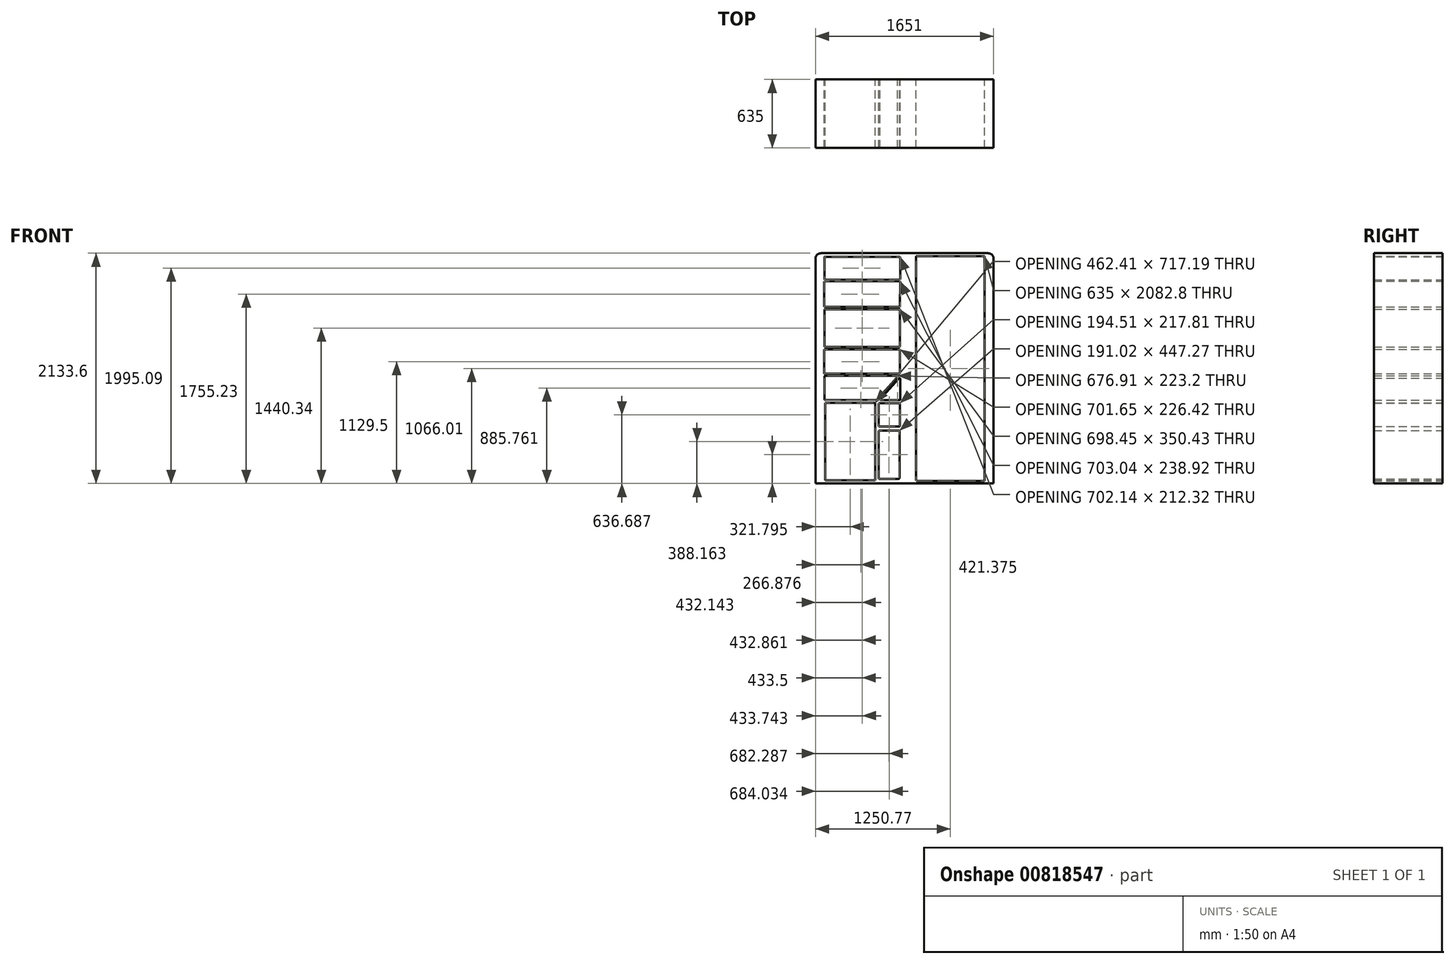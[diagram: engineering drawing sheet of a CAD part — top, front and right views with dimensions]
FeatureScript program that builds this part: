
annotation { "Feature Type Name" : "Feature", "Feature Type Description" : "" }
export const myFeature = defineFeature(function(context is Context, id is Id, definition is map)
    precondition{}
    {
        {
            var Q0;
            Q0=qCreatedBy(makeId("Front.planeOp"),FACE);
            var sketch = newSketch(context, id + "F0", { "sketchPlane" : qUnion([Q0])});
            skLineSegment(sketch, "E0.bottom", {"start": v(825.5, -1066.8) * mm, "end": v(-825.5, -1066.8) * mm});
            skLineSegment(sketch, "E0.top", {"start": v(774.7, 1066.8) * mm, "end": v(-774.7, 1066.8) * mm});
            skLineSegment(sketch, "E0.left", {"start": v(825.5, -1066.8) * mm, "end": v(825.5, 1016) * mm});
            skLineSegment(sketch, "E0.right", {"start": v(-825.5, -1066.8) * mm, "end": v(-825.5, 1016) * mm});
            skPoint(sketch, "E0.middle", {"position": v(0, 0) * mm});
            skLineSegment(sketch, "E1.bottom", {"start": v(114.12, 1040.61) * mm, "end": v(736.42, 1040.61) * mm});
            skLineSegment(sketch, "E1.top", {"start": v(114.12, -1042.19) * mm, "end": v(736.42, -1042.19) * mm});
            skLineSegment(sketch, "E1.left", {"start": v(107.77, 1034.26) * mm, "end": v(107.77, -1035.84) * mm});
            skLineSegment(sketch, "E1.right", {"start": v(742.77, 1034.26) * mm, "end": v(742.77, -1035.84) * mm});
            skPoint(sketch, "E2.oppositeSnap0", {"position": v(0, -1066.8) * mm});
            skLineSegment(sketch, "E2.bottom", {"start": v(-787.4, 1045.57) * mm, "end": v(0, 1045.57) * mm});
            skLineSegment(sketch, "E2.top", {"start": v(-787.4, -1037.23) * mm, "end": v(0, -1037.23) * mm});
            skLineSegment(sketch, "E2.left", {"start": v(-787.4, 1045.57) * mm, "end": v(-787.4, -1037.23) * mm});
            skLineSegment(sketch, "E2.right", {"start": v(0, 1045.57) * mm, "end": v(0, -1037.23) * mm});
            skLineSegment(sketch, "E3.bottom", {"start": v(-752.96, -302.88) * mm, "end": v(-32.15, -302.88) * mm});
            skLineSegment(sketch, "E3.top", {"start": v(-752.96, -1037.23) * mm, "end": v(-32.15, -1037.23) * mm});
            skLineSegment(sketch, "E3.left", {"start": v(-752.96, -302.88) * mm, "end": v(-752.96, -1037.23) * mm});
            skLineSegment(sketch, "E3.right", {"start": v(-32.15, -302.88) * mm, "end": v(-32.15, -1037.23) * mm});
            skLineSegment(sketch, "E4", {"start": v(-252.12, -302.88) * mm, "end": v(-252.12, -1037.23) * mm});
            skLineSegment(sketch, "E5", {"start": v(-252.12, -560.07) * mm, "end": v(-32.15, -560.07) * mm});
            skLineSegment(sketch, "E6.bottom", {"start": v(-752.96, 1045.57) * mm, "end": v(-32.15, 1045.57) * mm});
            skLineSegment(sketch, "E6.left", {"start": v(-752.96, 1045.57) * mm, "end": v(-752.96, -302.88) * mm});
            skLineSegment(sketch, "E6.right", {"start": v(-32.15, 1045.57) * mm, "end": v(-32.15, -302.88) * mm});
            skLineSegment(sketch, "E7", {"start": v(-752.96, 813.88) * mm, "end": v(-32.15, 813.88) * mm});
            skLineSegment(sketch, "E8", {"start": v(-752.96, 560.07) * mm, "end": v(-32.15, 560.07) * mm});
            skLineSegment(sketch, "E9", {"start": v(-752.96, 187.82) * mm, "end": v(-32.15, 187.82) * mm});
            skLineSegment(sketch, "E10", {"start": v(-752.96, -59.22) * mm, "end": v(-32.15, -59.22) * mm});
            skLineSegment(sketch, "E11", {"start": v(-252.12, -302.88) * mm, "end": v(-32.15, -59.22) * mm});
            skLineSegment(sketch, "E12.left", {"start": v(-752.96, 1016.92) * mm, "end": v(-752.96, 854.49) * mm});
            skLineSegment(sketch, "E12.right", {"start": v(-40.93, 1028.1) * mm, "end": v(-40.93, 828.48) * mm});
            skLineSegment(sketch, "E13.left", {"start": v(-752.96, 780.04) * mm, "end": v(-752.96, 593.91) * mm});
            skLineSegment(sketch, "E14.bottom", {"start": v(-734.63, 548.76) * mm, "end": v(-48.88, 548.76) * mm});
            skLineSegment(sketch, "E14.top", {"start": v(-734.63, 198.33) * mm, "end": v(-48.88, 198.33) * mm});
            skLineSegment(sketch, "E14.left", {"start": v(-740.98, 542.4) * mm, "end": v(-740.98, 204.68) * mm});
            skLineSegment(sketch, "E14.right", {"start": v(-42.53, 542.4) * mm, "end": v(-42.53, 204.68) * mm});
            skLineSegment(sketch, "E15.bottom", {"start": v(-737.83, 175.9) * mm, "end": v(-48.88, 175.9) * mm});
            skLineSegment(sketch, "E15.top", {"start": v(-737.83, -50.51) * mm, "end": v(-48.88, -50.51) * mm});
            skLineSegment(sketch, "E15.left", {"start": v(-744.18, 169.56) * mm, "end": v(-744.18, -44.16) * mm});
            skLineSegment(sketch, "E15.right", {"start": v(-42.53, 169.56) * mm, "end": v(-42.53, -44.16) * mm});
            skLineSegment(sketch, "E16.bottom", {"start": v(-728.56, -320.04) * mm, "end": v(-278.85, -320.04) * mm});
            skLineSegment(sketch, "E16.top", {"start": v(-734.9, -1037.23) * mm, "end": v(-272.5, -1037.23) * mm});
            skLineSegment(sketch, "E16.left", {"start": v(-734.9, -326.4) * mm, "end": v(-734.9, -1037.23) * mm});
            skLineSegment(sketch, "E16.right", {"start": v(-272.5, -326.4) * mm, "end": v(-272.5, -1037.23) * mm});
            skLineSegment(sketch, "E17.bottom", {"start": v(-232.37, -321.2) * mm, "end": v(-50.56, -321.2) * mm});
            skLineSegment(sketch, "E17.top", {"start": v(-232.37, -539.02) * mm, "end": v(-50.56, -539.02) * mm});
            skLineSegment(sketch, "E17.left", {"start": v(-238.72, -327.56) * mm, "end": v(-238.72, -532.67) * mm});
            skLineSegment(sketch, "E17.right", {"start": v(-44.2, -327.56) * mm, "end": v(-44.2, -532.67) * mm});
            skLineSegment(sketch, "E18.bottom", {"start": v(-232.37, -576.3) * mm, "end": v(-54.05, -576.3) * mm});
            skLineSegment(sketch, "E18.top", {"start": v(-232.37, -1023.56) * mm, "end": v(-54.05, -1023.56) * mm});
            skLineSegment(sketch, "E18.left", {"start": v(-238.72, -582.64) * mm, "end": v(-238.72, -1017.2) * mm});
            skLineSegment(sketch, "E18.right", {"start": v(-47.7, -582.64) * mm, "end": v(-47.7, -1017.2) * mm});
            skLineSegment(sketch, "E19", {"start": v(-742.58, -75.8) * mm, "end": v(-742.58, -286.29) * mm});
            skLineSegment(sketch, "E20", {"start": v(-736.23, -69.44) * mm, "end": v(-71.96, -69.44) * mm});
            skLineSegment(sketch, "E21", {"start": v(-67.25, -80.05) * mm, "end": v(-255.86, -288.97) * mm});
            skLineSegment(sketch, "E22", {"start": v(-260.56, -291.07) * mm, "end": v(-736.21, -292.64) * mm});
            skLineSegment(sketch, "E23", {"start": v(-40.13, -96.35) * mm, "end": v(-40.13, -286.34) * mm});
            skLineSegment(sketch, "E24", {"start": v(-51.2, -92.1) * mm, "end": v(-224.7, -284.28) * mm});
            skLineSegment(sketch, "E25", {"start": v(-46.4, -292.69) * mm, "end": v(-219.9, -294.88) * mm});
            skLineSegment(sketch, "E26", {"start": v(-47.28, 1034.45) * mm, "end": v(-736.72, 1034.45) * mm});
            skLineSegment(sketch, "E27", {"start": v(-743.07, 1028.1) * mm, "end": v(-743.07, 829.58) * mm});
            skLineSegment(sketch, "E28", {"start": v(-736.73, 823.23) * mm, "end": v(-47.3, 822.13) * mm});
            skLineSegment(sketch, "E29.right", {"start": v(-41.12, 801.53) * mm, "end": v(-41.71, 575.3) * mm});
            skLineSegment(sketch, "E30", {"start": v(-47.47, 807.9) * mm, "end": v(-736.92, 807.9) * mm});
            skLineSegment(sketch, "E31", {"start": v(-743.27, 801.57) * mm, "end": v(-744.16, 576.13) * mm});
            skLineSegment(sketch, "E32", {"start": v(-737.81, 569.76) * mm, "end": v(-48.07, 568.97) * mm});
            skPoint(sketch, "E33.visualSharp", {"position": v(825.5, 1066.8) * mm});
            skArc(sketch, "E33.filletArc", {"start": v(825.5, 1016) * mm, "mid": v(810.62, 1051.92) * mm, "end": v(774.7, 1066.8) * mm});
            skPoint(sketch, "E34.visualSharp", {"position": v(-825.5, 1066.8) * mm});
            skArc(sketch, "E34.filletArc", {"start": v(-774.7, 1066.8) * mm, "mid": v(-810.62, 1051.92) * mm, "end": v(-825.5, 1016) * mm});
            skPoint(sketch, "E35.visualSharp", {"position": v(-743.07, 1034.45) * mm});
            skArc(sketch, "E35.filletArc", {"start": v(-736.72, 1034.45) * mm, "mid": v(-741.21, 1032.59) * mm, "end": v(-743.07, 1028.1) * mm});
            skPoint(sketch, "E36.visualSharp", {"position": v(-743.07, 823.24) * mm});
            skArc(sketch, "E36.filletArc", {"start": v(-743.07, 829.58) * mm, "mid": v(-741.21, 825.1) * mm, "end": v(-736.73, 823.23) * mm});
            skPoint(sketch, "E37.visualSharp", {"position": v(-40.93, 1034.45) * mm});
            skArc(sketch, "E37.filletArc", {"start": v(-40.93, 1028.1) * mm, "mid": v(-42.8, 1032.59) * mm, "end": v(-47.28, 1034.45) * mm});
            skPoint(sketch, "E38.visualSharp", {"position": v(-40.93, 822.12) * mm});
            skArc(sketch, "E38.filletArc", {"start": v(-47.3, 822.13) * mm, "mid": v(-42.8, 823.98) * mm, "end": v(-40.93, 828.48) * mm});
            skPoint(sketch, "E39.visualSharp", {"position": v(-743.24, 807.9) * mm});
            skArc(sketch, "E39.filletArc", {"start": v(-736.92, 807.9) * mm, "mid": v(-741.4, 806.05) * mm, "end": v(-743.27, 801.57) * mm});
            skPoint(sketch, "E40.visualSharp", {"position": v(-744.18, 569.77) * mm});
            skArc(sketch, "E40.filletArc", {"start": v(-744.16, 576.13) * mm, "mid": v(-742.3, 571.63) * mm, "end": v(-737.81, 569.76) * mm});
            skPoint(sketch, "E41.visualSharp", {"position": v(-41.1, 807.9) * mm});
            skArc(sketch, "E41.filletArc", {"start": v(-41.12, 801.53) * mm, "mid": v(-42.97, 806.03) * mm, "end": v(-47.47, 807.9) * mm});
            skPoint(sketch, "E42.visualSharp", {"position": v(-41.73, 568.97) * mm});
            skArc(sketch, "E42.filletArc", {"start": v(-48.07, 568.97) * mm, "mid": v(-43.58, 570.82) * mm, "end": v(-41.71, 575.3) * mm});
            skPoint(sketch, "E43.visualSharp", {"position": v(-740.98, 198.33) * mm});
            skArc(sketch, "E43.filletArc", {"start": v(-740.98, 204.68) * mm, "mid": v(-739.12, 200.2) * mm, "end": v(-734.63, 198.33) * mm});
            skPoint(sketch, "E44.visualSharp", {"position": v(-740.98, 548.76) * mm});
            skArc(sketch, "E44.filletArc", {"start": v(-734.63, 548.76) * mm, "mid": v(-739.12, 546.9) * mm, "end": v(-740.98, 542.4) * mm});
            skPoint(sketch, "E45.visualSharp", {"position": v(-42.53, 548.76) * mm});
            skArc(sketch, "E45.filletArc", {"start": v(-42.53, 542.4) * mm, "mid": v(-44.4, 546.9) * mm, "end": v(-48.88, 548.76) * mm});
            skPoint(sketch, "E46.visualSharp", {"position": v(-42.53, 198.33) * mm});
            skArc(sketch, "E46.filletArc", {"start": v(-48.88, 198.33) * mm, "mid": v(-44.4, 200.2) * mm, "end": v(-42.53, 204.68) * mm});
            skPoint(sketch, "E47.visualSharp", {"position": v(-744.18, 175.9) * mm});
            skArc(sketch, "E47.filletArc", {"start": v(-737.83, 175.9) * mm, "mid": v(-742.32, 174.05) * mm, "end": v(-744.18, 169.56) * mm});
            skPoint(sketch, "E48.visualSharp", {"position": v(-42.53, 175.9) * mm});
            skArc(sketch, "E48.filletArc", {"start": v(-42.53, 169.56) * mm, "mid": v(-44.4, 174.05) * mm, "end": v(-48.88, 175.9) * mm});
            skPoint(sketch, "E49.visualSharp", {"position": v(-744.18, -50.51) * mm});
            skArc(sketch, "E49.filletArc", {"start": v(-744.18, -44.16) * mm, "mid": v(-742.32, -48.65) * mm, "end": v(-737.83, -50.51) * mm});
            skPoint(sketch, "E50.visualSharp", {"position": v(-42.53, -50.51) * mm});
            skArc(sketch, "E50.filletArc", {"start": v(-48.88, -50.51) * mm, "mid": v(-44.4, -48.65) * mm, "end": v(-42.53, -44.16) * mm});
            skPoint(sketch, "E51.visualSharp", {"position": v(-742.58, -69.44) * mm});
            skArc(sketch, "E51.filletArc", {"start": v(-736.23, -69.44) * mm, "mid": v(-740.72, -71.3) * mm, "end": v(-742.58, -75.8) * mm});
            skPoint(sketch, "E52.visualSharp", {"position": v(-742.58, -292.66) * mm});
            skArc(sketch, "E52.filletArc", {"start": v(-742.58, -286.29) * mm, "mid": v(-740.72, -290.78) * mm, "end": v(-736.21, -292.64) * mm});
            skPoint(sketch, "E53.visualSharp", {"position": v(-257.75, -291.06) * mm});
            skArc(sketch, "E53.filletArc", {"start": v(-260.56, -291.07) * mm, "mid": v(-257.99, -290.52) * mm, "end": v(-255.86, -288.97) * mm});
            skPoint(sketch, "E54.visualSharp", {"position": v(-57.68, -69.44) * mm});
            skArc(sketch, "E54.filletArc", {"start": v(-67.25, -80.05) * mm, "mid": v(-66.16, -73.21) * mm, "end": v(-71.96, -69.44) * mm});
            skPoint(sketch, "E55.visualSharp", {"position": v(-40.13, -79.84) * mm});
            skArc(sketch, "E55.filletArc", {"start": v(-40.13, -96.35) * mm, "mid": v(-44.2, -90.43) * mm, "end": v(-51.2, -92.1) * mm});
            skPoint(sketch, "E56.visualSharp", {"position": v(-234.43, -295.07) * mm});
            skArc(sketch, "E56.filletArc", {"start": v(-224.7, -284.28) * mm, "mid": v(-225.76, -291.15) * mm, "end": v(-219.9, -294.88) * mm});
            skPoint(sketch, "E57.visualSharp", {"position": v(-40.13, -292.6) * mm});
            skArc(sketch, "E57.filletArc", {"start": v(-46.4, -292.69) * mm, "mid": v(-41.96, -290.8) * mm, "end": v(-40.13, -286.34) * mm});
            skPoint(sketch, "E58.visualSharp", {"position": v(-734.9, -320.04) * mm});
            skArc(sketch, "E58.filletArc", {"start": v(-728.56, -320.04) * mm, "mid": v(-733.05, -321.9) * mm, "end": v(-734.9, -326.4) * mm});
            skPoint(sketch, "E59.visualSharp", {"position": v(-272.5, -320.04) * mm});
            skArc(sketch, "E59.filletArc", {"start": v(-272.5, -326.4) * mm, "mid": v(-274.36, -321.9) * mm, "end": v(-278.85, -320.04) * mm});
            skPoint(sketch, "E60.visualSharp", {"position": v(-238.72, -321.2) * mm});
            skArc(sketch, "E60.filletArc", {"start": v(-232.37, -321.2) * mm, "mid": v(-236.86, -323.07) * mm, "end": v(-238.72, -327.56) * mm});
            skPoint(sketch, "E61.visualSharp", {"position": v(-238.72, -539.02) * mm});
            skArc(sketch, "E61.filletArc", {"start": v(-238.72, -532.67) * mm, "mid": v(-236.86, -537.16) * mm, "end": v(-232.37, -539.02) * mm});
            skPoint(sketch, "E62.visualSharp", {"position": v(-44.2, -321.2) * mm});
            skArc(sketch, "E62.filletArc", {"start": v(-44.2, -327.56) * mm, "mid": v(-46.07, -323.07) * mm, "end": v(-50.56, -321.2) * mm});
            skPoint(sketch, "E63.visualSharp", {"position": v(-44.2, -539.02) * mm});
            skArc(sketch, "E63.filletArc", {"start": v(-50.56, -539.02) * mm, "mid": v(-46.07, -537.16) * mm, "end": v(-44.2, -532.67) * mm});
            skPoint(sketch, "E64.visualSharp", {"position": v(-238.72, -576.3) * mm});
            skArc(sketch, "E64.filletArc", {"start": v(-232.37, -576.3) * mm, "mid": v(-236.86, -578.15) * mm, "end": v(-238.72, -582.64) * mm});
            skPoint(sketch, "E65.visualSharp", {"position": v(-47.7, -576.3) * mm});
            skArc(sketch, "E65.filletArc", {"start": v(-47.7, -582.64) * mm, "mid": v(-49.56, -578.15) * mm, "end": v(-54.05, -576.3) * mm});
            skPoint(sketch, "E66.visualSharp", {"position": v(-238.72, -1023.56) * mm});
            skArc(sketch, "E66.filletArc", {"start": v(-238.72, -1017.2) * mm, "mid": v(-236.86, -1021.7) * mm, "end": v(-232.37, -1023.56) * mm});
            skPoint(sketch, "E67.visualSharp", {"position": v(-47.7, -1023.56) * mm});
            skArc(sketch, "E67.filletArc", {"start": v(-54.05, -1023.56) * mm, "mid": v(-49.56, -1021.7) * mm, "end": v(-47.7, -1017.2) * mm});
            skPoint(sketch, "E68.visualSharp", {"position": v(107.77, 1040.61) * mm});
            skArc(sketch, "E68.filletArc", {"start": v(114.12, 1040.61) * mm, "mid": v(109.63, 1038.75) * mm, "end": v(107.77, 1034.26) * mm});
            skPoint(sketch, "E69.visualSharp", {"position": v(742.77, 1040.61) * mm});
            skArc(sketch, "E69.filletArc", {"start": v(742.77, 1034.26) * mm, "mid": v(740.91, 1038.75) * mm, "end": v(736.42, 1040.61) * mm});
            skPoint(sketch, "E70.visualSharp", {"position": v(107.77, -1042.19) * mm});
            skArc(sketch, "E70.filletArc", {"start": v(107.77, -1035.84) * mm, "mid": v(109.63, -1040.33) * mm, "end": v(114.12, -1042.19) * mm});
            skPoint(sketch, "E71.visualSharp", {"position": v(742.77, -1042.19) * mm});
            skArc(sketch, "E71.filletArc", {"start": v(736.42, -1042.19) * mm, "mid": v(740.91, -1040.33) * mm, "end": v(742.77, -1035.84) * mm});
            skSolve(sketch);
        }
        {
            var Q0;
            Q0=makeQuery(id+"F0.imprint","IMPRINT",FACE,{"disambiguationData":[TD([[makeQuery(id+"F0.imprint","IMPRINT",EDGE,{"derivedFrom":sQuery(id+"F0.wireOp",EDGE,"E0.bottom")}),-1.0]])]});
            var Q1;
            {var subQ11=sQuery(id+"F0.wireOp",EDGE,"E2.left");Q1=makeQuery(id+"F0.imprint","IMPRINT",FACE,{"disambiguationData":[TD([[makeQuery(id+"F0.imprint","IMPRINT",EDGE,{"derivedFrom":subQ11}),1.0]])]});}
            var Q2;
            {var subQ8=sQuery(id+"F0.wireOp",EDGE,"E3.left");Q2=makeQuery(id+"F0.imprint","IMPRINT",FACE,{"disambiguationData":[TD([[makeQuery(id+"F0.imprint","IMPRINT",EDGE,{"derivedFrom":subQ8}),1.0]])]});}
            var Q3;
            {var subQ5=sQuery(id+"F0.wireOp",EDGE,"E5");Q3=makeQuery(id+"F0.imprint","IMPRINT",FACE,{"disambiguationData":[TD([[makeQuery(id+"F0.imprint","IMPRINT",EDGE,{"derivedFrom":subQ5}),1.0]])]});}
            var Q4;
            {var subQ5=sQuery(id+"F0.wireOp",EDGE,"E5");Q4=makeQuery(id+"F0.imprint","IMPRINT",FACE,{"disambiguationData":[TD([[makeQuery(id+"F0.imprint","IMPRINT",EDGE,{"derivedFrom":subQ5}),-1.0]])]});}
            var Q5;
            {var subQ3=sQuery(id+"F0.wireOp",EDGE,"E10");Q5=makeQuery(id+"F0.imprint","IMPRINT",FACE,{"disambiguationData":[TD([[makeQuery(id+"F0.imprint","IMPRINT",EDGE,{"derivedFrom":subQ3}),-1.0]])]});}
            var Q6;
            {var subQ3=sQuery(id+"F0.wireOp",EDGE,"E11");Q6=makeQuery(id+"F0.imprint","IMPRINT",FACE,{"disambiguationData":[TD([[makeQuery(id+"F0.imprint","IMPRINT",EDGE,{"derivedFrom":subQ3}),-1.0]])]});}
            var Q7;
            {var subQ0=sQuery(id+"F0.wireOp",EDGE,"E9");Q7=makeQuery(id+"F0.imprint","IMPRINT",FACE,{"disambiguationData":[TD([[makeQuery(id+"F0.imprint","IMPRINT",EDGE,{"derivedFrom":subQ0}),-1.0]])]});}
            var Q8;
            {var subQ0=sQuery(id+"F0.wireOp",EDGE,"E8");Q8=makeQuery(id+"F0.imprint","IMPRINT",FACE,{"disambiguationData":[TD([[makeQuery(id+"F0.imprint","IMPRINT",EDGE,{"derivedFrom":subQ0}),-1.0]])]});}
            var Q9;
            {var subQ0=sQuery(id+"F0.wireOp",EDGE,"E7");Q9=makeQuery(id+"F0.imprint","IMPRINT",FACE,{"disambiguationData":[TD([[makeQuery(id+"F0.imprint","IMPRINT",EDGE,{"derivedFrom":subQ0}),-1.0]])]});}
            var Q10;
            {var subQ4=sQuery(id+"F0.wireOp",EDGE,"E2.right");Q10=makeQuery(id+"F0.imprint","IMPRINT",FACE,{"disambiguationData":[TD([[makeQuery(id+"F0.imprint","IMPRINT",EDGE,{"derivedFrom":subQ4}),-1.0]])]});}
            var Q11;
            {var subQ0=sQuery(id+"F0.wireOp",EDGE,"E7");Q11=makeQuery(id+"F0.imprint","IMPRINT",FACE,{"disambiguationData":[TD([[makeQuery(id+"F0.imprint","IMPRINT",EDGE,{"derivedFrom":subQ0}),1.0]])]});}
            extrude(context, id + "F1", {"entities" : qUnion([Q0, Q1, Q2, Q3, Q4, Q5, Q6, Q7, Q8, Q9, Q10, Q11]), "depth" : 635 * mm, "offsetDistance" : 25.4 * mm});
        }
    });
